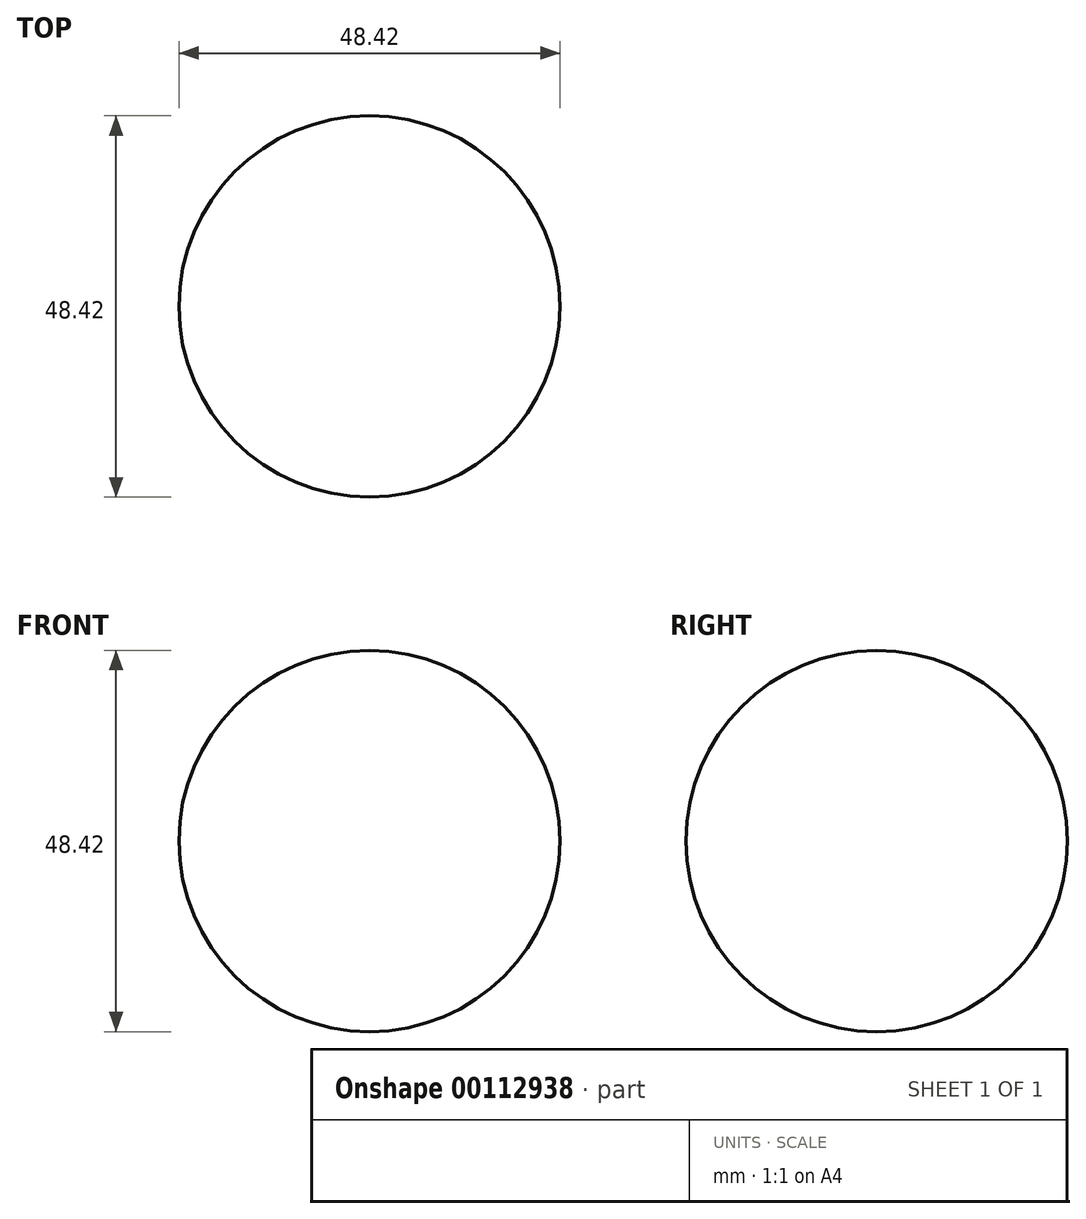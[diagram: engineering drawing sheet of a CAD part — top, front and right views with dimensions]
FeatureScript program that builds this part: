
annotation { "Feature Type Name" : "Feature", "Feature Type Description" : "" }
export const myFeature = defineFeature(function(context is Context, id is Id, definition is map)
    precondition{}
    {
        {
            var Q0;
            Q0=qCreatedBy(makeId("Front.planeOp"),FACE);
            var sketch = newSketch(context, id + "F0", { "sketchPlane" : qUnion([Q0])});
            skArc(sketch, "E0", {"start": v(24.21, 0) * mm, "mid": v(0, 24.21) * mm, "end": v(-24.21, 0) * mm});
            skLineSegment(sketch, "E1", {"start": v(-24.21, 0) * mm, "end": v(24.21, 0) * mm});
            skPoint(sketch, "E2.orphan", {"position": v(-31.66, 0) * mm});
            skSolve(sketch);
        }
        {
            var Q0;
            Q0 = qSketchRegion(id + "F0", true);
            var Q1;
            Q1=sQuery(id+"F0.wireOp",EDGE,"E1");
            revolve(context, id + "F1", {"entities" : qUnion([Q0]), "axis" : qUnion([Q1]), "revolveType" : RevolveType.FULL});
        }
    });
